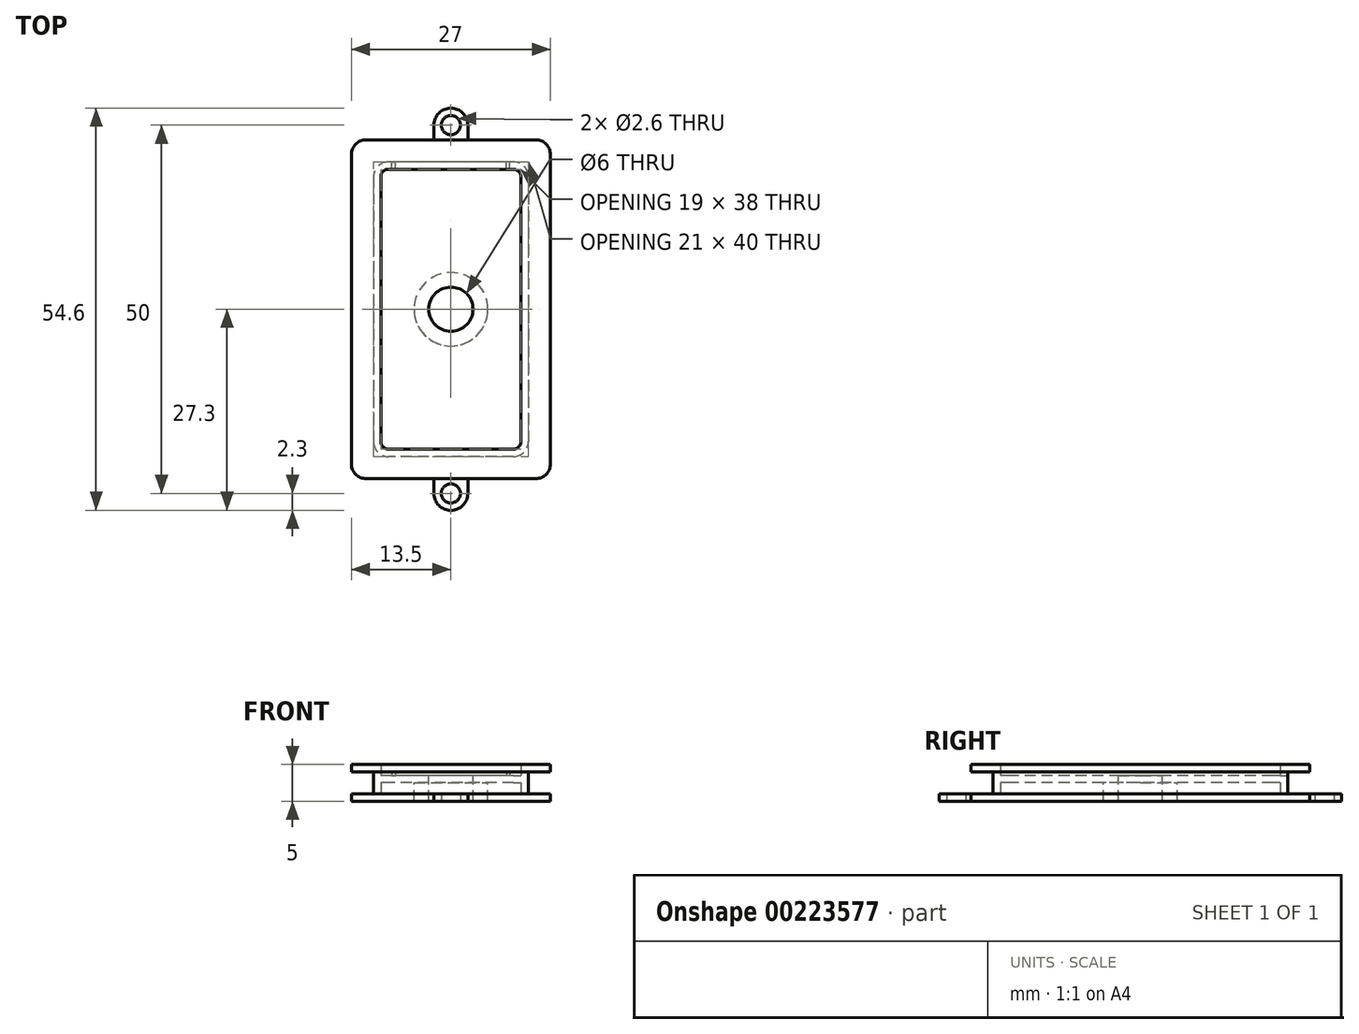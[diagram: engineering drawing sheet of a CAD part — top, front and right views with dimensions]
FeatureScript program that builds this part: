
annotation { "Feature Type Name" : "Feature", "Feature Type Description" : "" }
export const myFeature = defineFeature(function(context is Context, id is Id, definition is map)
    precondition{}
    {
        {
            var Q0;
            Q0=qCreatedBy(makeId("Top.planeOp"),FACE);
            var sketch = newSketch(context, id + "F0", { "sketchPlane" : qUnion([Q0])});
            skLineSegment(sketch, "E0.bottom", {"start": v(11.5, 23) * mm, "end": v(-11.5, 23) * mm});
            skLineSegment(sketch, "E0.top", {"start": v(11.5, -23) * mm, "end": v(-11.5, -23) * mm});
            skLineSegment(sketch, "E0.left", {"start": v(13.5, 21) * mm, "end": v(13.5, -21) * mm});
            skLineSegment(sketch, "E0.right", {"start": v(-13.5, 21) * mm, "end": v(-13.5, -21) * mm});
            skPoint(sketch, "E0.middle", {"position": v(0, 0) * mm});
            skPoint(sketch, "E1.visualSharp", {"position": v(-13.5, 23) * mm});
            skArc(sketch, "E1.filletArc", {"start": v(-11.5, 23) * mm, "mid": v(-12.91, 22.41) * mm, "end": v(-13.5, 21) * mm});
            skPoint(sketch, "E2.visualSharp", {"position": v(13.5, 23) * mm});
            skArc(sketch, "E2.filletArc", {"start": v(13.5, 21) * mm, "mid": v(12.91, 22.41) * mm, "end": v(11.5, 23) * mm});
            skPoint(sketch, "E3.visualSharp", {"position": v(13.5, -23) * mm});
            skArc(sketch, "E3.filletArc", {"start": v(11.5, -23) * mm, "mid": v(12.91, -22.41) * mm, "end": v(13.5, -21) * mm});
            skPoint(sketch, "E4.visualSharp", {"position": v(-13.5, -23) * mm});
            skArc(sketch, "E4.filletArc", {"start": v(-13.5, -21) * mm, "mid": v(-12.91, -22.41) * mm, "end": v(-11.5, -23) * mm});
            skSolve(sketch);
        }
        {
            var Q0;
            Q0=makeQuery(id+"F0.imprint","IMPRINT",FACE,{"disambiguationData":[TD([[makeQuery(id+"F0.imprint","IMPRINT",EDGE,{"derivedFrom":sQuery(id+"F0.wireOp",EDGE,"E0.bottom")}),1.0]])]});
            extrude(context, id + "F1", {"entities" : qUnion([Q0]), "depth" : 1 * mm});
        }
        {
            var Q0;
            Q0=makeQuery(id+"F1.opExtrude","CAP_FACE",FACE,{"disambiguationData":[OSD([sQuery(id+"F0.wireOp",EDGE,"E0.bottom"),sQuery(id+"F0.wireOp",EDGE,"E0.top"),sQuery(id+"F0.wireOp",EDGE,"E0.left"),sQuery(id+"F0.wireOp",EDGE,"E0.right"),sQuery(id+"F0.wireOp",EDGE,"E1.filletArc"),sQuery(id+"F0.wireOp",EDGE,"E2.filletArc"),sQuery(id+"F0.wireOp",EDGE,"E3.filletArc"),sQuery(id+"F0.wireOp",EDGE,"E4.filletArc")])],"isStart":false});
            var sketch = newSketch(context, id + "F2", { "sketchPlane" : qUnion([Q0])});
            skLineSegment(sketch, "E5.0", {"start": v(8.5, 20) * mm, "end": v(-8.5, 20) * mm});
            skLineSegment(sketch, "E5.1", {"start": v(10.5, 18) * mm, "end": v(10.5, -18) * mm});
            skLineSegment(sketch, "E5.2", {"start": v(8.5, -20) * mm, "end": v(-8.5, -20) * mm});
            skLineSegment(sketch, "E5.3", {"start": v(-10.5, 18) * mm, "end": v(-10.5, -18) * mm});
            skPoint(sketch, "E6.visualSharp", {"position": v(-10.5, 20) * mm});
            skArc(sketch, "E6.filletArc", {"start": v(-8.5, 20) * mm, "mid": v(-9.91, 19.41) * mm, "end": v(-10.5, 18) * mm});
            skPoint(sketch, "E7.visualSharp", {"position": v(10.5, 20) * mm});
            skArc(sketch, "E7.filletArc", {"start": v(10.5, 18) * mm, "mid": v(9.91, 19.41) * mm, "end": v(8.5, 20) * mm});
            skPoint(sketch, "E8.visualSharp", {"position": v(10.5, -20) * mm});
            skArc(sketch, "E8.filletArc", {"start": v(8.5, -20) * mm, "mid": v(9.91, -19.41) * mm, "end": v(10.5, -18) * mm});
            skPoint(sketch, "E9.visualSharp", {"position": v(-10.5, -20) * mm});
            skArc(sketch, "E9.filletArc", {"start": v(-10.5, -18) * mm, "mid": v(-9.91, -19.41) * mm, "end": v(-8.5, -20) * mm});
            skArc(sketch, "E10.0", {"start": v(9.5, 18) * mm, "mid": v(9.2, 18.7) * mm, "end": v(8.5, 19) * mm});
            skLineSegment(sketch, "E10.1", {"start": v(9.5, 18) * mm, "end": v(9.5, -18) * mm});
            skLineSegment(sketch, "E10.2", {"start": v(8.5, 19) * mm, "end": v(-8.5, 19) * mm});
            skArc(sketch, "E10.3", {"start": v(8.5, -19) * mm, "mid": v(9.2, -18.7) * mm, "end": v(9.5, -18) * mm});
            skArc(sketch, "E10.4", {"start": v(-8.5, 19) * mm, "mid": v(-9.2, 18.7) * mm, "end": v(-9.5, 18) * mm});
            skLineSegment(sketch, "E10.5", {"start": v(-9.5, 18) * mm, "end": v(-9.5, -18) * mm});
            skArc(sketch, "E10.6", {"start": v(-9.5, -18) * mm, "mid": v(-9.2, -18.7) * mm, "end": v(-8.5, -19) * mm});
            skLineSegment(sketch, "E10.7", {"start": v(8.5, -19) * mm, "end": v(-8.5, -19) * mm});
            skSolve(sketch);
        }
        {
            var Q0;
            Q0 = qSketchRegion(id + "F2", true);
            extrude(context, id + "F3", {"entities" : qUnion([Q0]), "operationType" : NewBodyOperationType.ADD, "depth" : 3 * mm});
        }
        {
            var Q0;
            Q0=makeQuery(id+"F3.boolean.opBoolean","SPLIT",FACE,{"disambiguationData":[TD([makeQuery(id+"F3.opExtrude","SWEPT_FACE",FACE,{"disambiguationData":[OSD([sQuery(id+"F2.wireOp",EDGE,"E10.0")])]})])],"derivedFrom":makeQuery(id+"F1.opExtrude","CAP_FACE",FACE,{"disambiguationData":[OSD([sQuery(id+"F0.wireOp",EDGE,"E0.bottom"),sQuery(id+"F0.wireOp",EDGE,"E0.top"),sQuery(id+"F0.wireOp",EDGE,"E0.left"),sQuery(id+"F0.wireOp",EDGE,"E0.right"),sQuery(id+"F0.wireOp",EDGE,"E1.filletArc"),sQuery(id+"F0.wireOp",EDGE,"E2.filletArc"),sQuery(id+"F0.wireOp",EDGE,"E3.filletArc"),sQuery(id+"F0.wireOp",EDGE,"E4.filletArc")])],"isStart":false})});
            extrude(context, id + "F4", {"entities" : qUnion([Q0]), "operationType" : NewBodyOperationType.REMOVE, "endBound" : BoundingType.THROUGH_ALL, "oppositeDirection" : true, "depth" : 25 * mm});
        }
        {
            var Q0;
            Q0=makeQuery(id+"F3.opExtrude","CAP_FACE",FACE,{"disambiguationData":[OSD([sQuery(id+"F2.wireOp",EDGE,"E5.0"),sQuery(id+"F2.wireOp",EDGE,"E5.1"),sQuery(id+"F2.wireOp",EDGE,"E5.2"),sQuery(id+"F2.wireOp",EDGE,"E5.3"),sQuery(id+"F2.wireOp",EDGE,"E6.filletArc"),sQuery(id+"F2.wireOp",EDGE,"E7.filletArc"),sQuery(id+"F2.wireOp",EDGE,"E8.filletArc"),sQuery(id+"F2.wireOp",EDGE,"E9.filletArc"),sQuery(id+"F2.wireOp",EDGE,"E10.0"),sQuery(id+"F2.wireOp",EDGE,"E10.1"),sQuery(id+"F2.wireOp",EDGE,"E10.2"),sQuery(id+"F2.wireOp",EDGE,"E10.3"),sQuery(id+"F2.wireOp",EDGE,"E10.4"),sQuery(id+"F2.wireOp",EDGE,"E10.5"),sQuery(id+"F2.wireOp",EDGE,"E10.6"),sQuery(id+"F2.wireOp",EDGE,"E10.7")])],"isStart":false});
            var sketch = newSketch(context, id + "F5", { "sketchPlane" : qUnion([Q0])});
            skArc(sketch, "E11.0", {"start": v(9.5, 18) * mm, "mid": v(9.2, 18.7) * mm, "end": v(8.5, 19) * mm});
            skLineSegment(sketch, "E11.1", {"start": v(9.5, 18) * mm, "end": v(9.5, -18) * mm});
            skLineSegment(sketch, "E11.2", {"start": v(8.5, 19) * mm, "end": v(-8.5, 19) * mm});
            skArc(sketch, "E11.3", {"start": v(8.5, -19) * mm, "mid": v(9.2, -18.7) * mm, "end": v(9.5, -18) * mm});
            skArc(sketch, "E11.4", {"start": v(-8.5, 19) * mm, "mid": v(-9.2, 18.7) * mm, "end": v(-9.5, 18) * mm});
            skLineSegment(sketch, "E11.5", {"start": v(-9.5, 18) * mm, "end": v(-9.5, -18) * mm});
            skArc(sketch, "E11.6", {"start": v(-9.5, -18) * mm, "mid": v(-9.2, -18.7) * mm, "end": v(-8.5, -19) * mm});
            skLineSegment(sketch, "E11.7", {"start": v(8.5, -19) * mm, "end": v(-8.5, -19) * mm});
            skArc(sketch, "E12.0", {"start": v(13.5, 21) * mm, "mid": v(12.91, 22.41) * mm, "end": v(11.5, 23) * mm});
            skLineSegment(sketch, "E12.1", {"start": v(11.5, 23) * mm, "end": v(-11.5, 23) * mm});
            skLineSegment(sketch, "E12.2", {"start": v(13.5, 21) * mm, "end": v(13.5, -21) * mm});
            skArc(sketch, "E12.3", {"start": v(-11.5, 23) * mm, "mid": v(-12.91, 22.41) * mm, "end": v(-13.5, 21) * mm});
            skArc(sketch, "E12.4", {"start": v(11.5, -23) * mm, "mid": v(12.91, -22.41) * mm, "end": v(13.5, -21) * mm});
            skLineSegment(sketch, "E12.5", {"start": v(11.5, -23) * mm, "end": v(-11.5, -23) * mm});
            skArc(sketch, "E12.6", {"start": v(-13.5, -21) * mm, "mid": v(-12.91, -22.41) * mm, "end": v(-11.5, -23) * mm});
            skLineSegment(sketch, "E12.7", {"start": v(-13.5, 21) * mm, "end": v(-13.5, -21) * mm});
            skSolve(sketch);
        }
        {
            var Q0;
            Q0 = qSketchRegion(id + "F5", true);
            extrude(context, id + "F6", {"entities" : qUnion([Q0]), "operationType" : NewBodyOperationType.ADD, "depth" : 1 * mm});
        }
        {
            var Q0;
            Q0=qCreatedBy(makeId("Top.planeOp"),FACE);
            var sketch = newSketch(context, id + "F7", { "sketchPlane" : qUnion([Q0])});
            skCircle(sketch, "E13", {"center": v(0, 25) * mm, "radius": 1.3 * mm});
            skArc(sketch, "E14", {"start": v(2.3, 25) * mm, "mid": v(0, 27.3) * mm, "end": v(-2.3, 25) * mm});
            skLineSegment(sketch, "E15", {"start": v(-2.3, 25) * mm, "end": v(-2.3, 23) * mm});
            skLineSegment(sketch, "E16", {"start": v(2.3, 25) * mm, "end": v(2.3, 23) * mm});
            skLineSegment(sketch, "E17", {"start": v(-2.3, 23) * mm, "end": v(2.3, 23) * mm});
            skLineSegment(sketch, "E18.MirrorCS", {"start": v(2.3, -25) * mm, "end": v(2.3, -23) * mm});
            skLineSegment(sketch, "E19.MirrorCS", {"start": v(-2.3, -25) * mm, "end": v(-2.3, -23) * mm});
            skCircle(sketch, "E20.MirrorC", {"center": v(0, -25) * mm, "radius": 1.3 * mm});
            skLineSegment(sketch, "E21.MirrorCS", {"start": v(-2.3, -23) * mm, "end": v(2.3, -23) * mm});
            skArc(sketch, "E22.MirrorCS", {"start": v(2.3, -25) * mm, "mid": v(0, -27.3) * mm, "end": v(-2.3, -25) * mm});
            skSolve(sketch);
        }
        {
            var Q0;
            Q0 = qSketchRegion(id + "F7", true);
            extrude(context, id + "F8", {"entities" : qUnion([Q0]), "operationType" : NewBodyOperationType.ADD, "depth" : 1 * mm});
        }
        {
            var Q0;
            Q0=makeQuery(id+"F6.opExtrude","CAP_FACE",FACE,{"disambiguationData":[OSD([sQuery(id+"F5.wireOp",EDGE,"E11.0"),sQuery(id+"F5.wireOp",EDGE,"E11.1"),sQuery(id+"F5.wireOp",EDGE,"E11.2"),sQuery(id+"F5.wireOp",EDGE,"E11.3"),sQuery(id+"F5.wireOp",EDGE,"E11.4"),sQuery(id+"F5.wireOp",EDGE,"E11.5"),sQuery(id+"F5.wireOp",EDGE,"E11.6"),sQuery(id+"F5.wireOp",EDGE,"E11.7"),sQuery(id+"F5.wireOp",EDGE,"E12.0"),sQuery(id+"F5.wireOp",EDGE,"E12.1"),sQuery(id+"F5.wireOp",EDGE,"E12.2"),sQuery(id+"F5.wireOp",EDGE,"E12.3"),sQuery(id+"F5.wireOp",EDGE,"E12.4"),sQuery(id+"F5.wireOp",EDGE,"E12.5"),sQuery(id+"F5.wireOp",EDGE,"E12.6"),sQuery(id+"F5.wireOp",EDGE,"E12.7")])],"isStart":true});
            var Q1;
            {var subQ0=sQuery(id+"F0.wireOp",EDGE,"E4.filletArc");var subQ1=sQuery(id+"F0.wireOp",EDGE,"E3.filletArc");var subQ2=sQuery(id+"F0.wireOp",EDGE,"E2.filletArc");var subQ3=sQuery(id+"F0.wireOp",EDGE,"E1.filletArc");var subQ4=sQuery(id+"F0.wireOp",EDGE,"E0.bottom");var subQ5=sQuery(id+"F0.wireOp",EDGE,"E0.top");var subQ6=sQuery(id+"F0.wireOp",EDGE,"E0.left");var subQ7=sQuery(id+"F0.wireOp",EDGE,"E0.right");Q1=makeQuery(id+"F8.boolean.opBoolean","MERGE",FACE,{"derivedFrom":[makeQuery(id+"F3.boolean.opBoolean","SPLIT",FACE,{"disambiguationData":[TD([makeQuery(id+"F1.opExtrude","SWEPT_FACE",FACE,{"disambiguationData":[OSD([subQ4])]})])],"derivedFrom":makeQuery(id+"F1.opExtrude","CAP_FACE",FACE,{"disambiguationData":[OSD([subQ4,subQ5,subQ6,subQ7,subQ3,subQ2,subQ1,subQ0])],"isStart":false})}),makeQuery(id+"F8.opExtrude","CAP_FACE",FACE,{"disambiguationData":[OSD([sQuery(id+"F7.wireOp",EDGE,"E13"),sQuery(id+"F7.wireOp",EDGE,"E14"),sQuery(id+"F7.wireOp",EDGE,"E15"),sQuery(id+"F7.wireOp",EDGE,"E16"),sQuery(id+"F7.wireOp",EDGE,"E17")])],"isStart":false}),makeQuery(id+"F8.opExtrude","CAP_FACE",FACE,{"disambiguationData":[OSD([sQuery(id+"F7.wireOp",EDGE,"E18.MirrorCS"),sQuery(id+"F7.wireOp",EDGE,"E19.MirrorCS"),sQuery(id+"F7.wireOp",EDGE,"E20.MirrorC"),sQuery(id+"F7.wireOp",EDGE,"E21.MirrorCS"),sQuery(id+"F7.wireOp",EDGE,"E22.MirrorCS")])],"isStart":false})]});}
            cPlane(context, id + "F9", {"entities" : qUnion([Q0, Q1]), "cplaneType" : CPlaneType.MID_PLANE, "offset" : 25 * mm, "width" : 150 * mm, "height" : 150 * mm});
        }
        {
            var Q0;
            Q0=qCreatedBy(id+"F9.planeOp",FACE);
            var sketch = newSketch(context, id + "F10", { "sketchPlane" : qUnion([Q0])});
            skLineSegment(sketch, "E23.0", {"start": v(9.5, -19) * mm, "end": v(-9.5, -19) * mm});
            skLineSegment(sketch, "E23.1", {"start": v(9.5, -19) * mm, "end": v(9.5, 19) * mm});
            skLineSegment(sketch, "E23.2", {"start": v(9.5, 19) * mm, "end": v(-9.5, 19) * mm});
            skLineSegment(sketch, "E23.3", {"start": v(-9.5, -19) * mm, "end": v(-9.5, 19) * mm});
            skSolve(sketch);
        }
        {
            var Q0;
            Q0 = qSketchRegion(id + "F10", true);
            extrude(context, id + "F11", {"entities" : qUnion([Q0]), "operationType" : NewBodyOperationType.ADD, "oppositeDirection" : true, "depth" : 1 * mm});
        }
        {
            var Q0;
            Q0=makeQuery(id+"F11.opExtrude","CAP_FACE",FACE,{"disambiguationData":[OSD([sQuery(id+"F10.wireOp",EDGE,"E23.0"),sQuery(id+"F10.wireOp",EDGE,"E23.1"),sQuery(id+"F10.wireOp",EDGE,"E23.2"),sQuery(id+"F10.wireOp",EDGE,"E23.3")])],"isStart":false});
            var sketch = newSketch(context, id + "F12", { "sketchPlane" : qUnion([Q0])});
            skCircle(sketch, "E24", {"center": v(0, 0) * mm, "radius": 3 * mm});
            skSolve(sketch);
        }
        {
            var Q0;
            Q0 = qSketchRegion(id + "F12", true);
            extrude(context, id + "F13", {"entities" : qUnion([Q0]), "operationType" : NewBodyOperationType.REMOVE, "oppositeDirection" : true, "depth" : 25 * mm});
        }
        {
            var Q0;
            Q0=makeQuery(id+"F11.opExtrude","CAP_FACE",FACE,{"disambiguationData":[OSD([sQuery(id+"F10.wireOp",EDGE,"E23.0"),sQuery(id+"F10.wireOp",EDGE,"E23.1"),sQuery(id+"F10.wireOp",EDGE,"E23.2"),sQuery(id+"F10.wireOp",EDGE,"E23.3")])],"isStart":true});
            var sketch = newSketch(context, id + "F14", { "sketchPlane" : qUnion([Q0])});
            skCircle(sketch, "E25", {"center": v(0, 0) * mm, "radius": 3 * mm});
            skCircle(sketch, "E26", {"center": v(0, 0) * mm, "radius": 5 * mm});
            skSolve(sketch);
        }
        {
            var Q0;
            Q0 = qSketchRegion(id + "F14", true);
            var Q1;
            Q1=makeQuery(id+"F8.boolean.opBoolean","MERGE",FACE,{"derivedFrom":[makeQuery(id+"F1.opExtrude","CAP_FACE",FACE,{"disambiguationData":[OSD([sQuery(id+"F0.wireOp",EDGE,"E0.bottom"),sQuery(id+"F0.wireOp",EDGE,"E0.top"),sQuery(id+"F0.wireOp",EDGE,"E0.left"),sQuery(id+"F0.wireOp",EDGE,"E0.right"),sQuery(id+"F0.wireOp",EDGE,"E1.filletArc"),sQuery(id+"F0.wireOp",EDGE,"E2.filletArc"),sQuery(id+"F0.wireOp",EDGE,"E3.filletArc"),sQuery(id+"F0.wireOp",EDGE,"E4.filletArc")])],"isStart":true}),makeQuery(id+"F8.opExtrude","CAP_FACE",FACE,{"disambiguationData":[OSD([sQuery(id+"F7.wireOp",EDGE,"E13"),sQuery(id+"F7.wireOp",EDGE,"E14"),sQuery(id+"F7.wireOp",EDGE,"E15"),sQuery(id+"F7.wireOp",EDGE,"E16"),sQuery(id+"F7.wireOp",EDGE,"E17")])],"isStart":true}),makeQuery(id+"F8.opExtrude","CAP_FACE",FACE,{"disambiguationData":[OSD([sQuery(id+"F7.wireOp",EDGE,"E18.MirrorCS"),sQuery(id+"F7.wireOp",EDGE,"E19.MirrorCS"),sQuery(id+"F7.wireOp",EDGE,"E20.MirrorC"),sQuery(id+"F7.wireOp",EDGE,"E21.MirrorCS"),sQuery(id+"F7.wireOp",EDGE,"E22.MirrorCS")])],"isStart":true})]});
            extrude(context, id + "F15", {"entities" : qUnion([Q0]), "operationType" : NewBodyOperationType.ADD, "endBound" : BoundingType.UP_TO_SURFACE, "endBoundEntityFace" : qUnion([Q1]), "depth" : 25 * mm});
        }
        {
            var Q0;
            Q0=makeQuery(id+"F3.opExtrude","SWEPT_FACE",FACE,{"disambiguationData":[OSD([sQuery(id+"F2.wireOp",EDGE,"E5.0")])]});
            var sketch = newSketch(context, id + "F16", { "sketchPlane" : qUnion([Q0])});
            skLineSegment(sketch, "E27.bottom", {"start": v(-8, 3.5) * mm, "end": v(-7.5, 3.5) * mm});
            skLineSegment(sketch, "E27.top", {"start": v(-8, 4) * mm, "end": v(-7.5, 4) * mm});
            skLineSegment(sketch, "E27.left", {"start": v(-8, 3.5) * mm, "end": v(-8, 4) * mm});
            skLineSegment(sketch, "E27.right", {"start": v(-7.5, 3.5) * mm, "end": v(-7.5, 4) * mm});
            skLineSegment(sketch, "E28.MirrorCS", {"start": v(7.5, 3.5) * mm, "end": v(7.5, 4) * mm});
            skLineSegment(sketch, "E29.MirrorCS", {"start": v(8, 3.5) * mm, "end": v(8, 4) * mm});
            skLineSegment(sketch, "E30.MirrorCS", {"start": v(8, 4) * mm, "end": v(7.5, 4) * mm});
            skLineSegment(sketch, "E31.MirrorCS", {"start": v(8, 3.5) * mm, "end": v(7.5, 3.5) * mm});
            skSolve(sketch);
        }
        {
            var Q0;
            Q0 = qSketchRegion(id + "F16", true);
            extrude(context, id + "F17", {"entities" : qUnion([Q0]), "operationType" : NewBodyOperationType.REMOVE, "oppositeDirection" : true, "depth" : 5 * mm});
        }
    });
